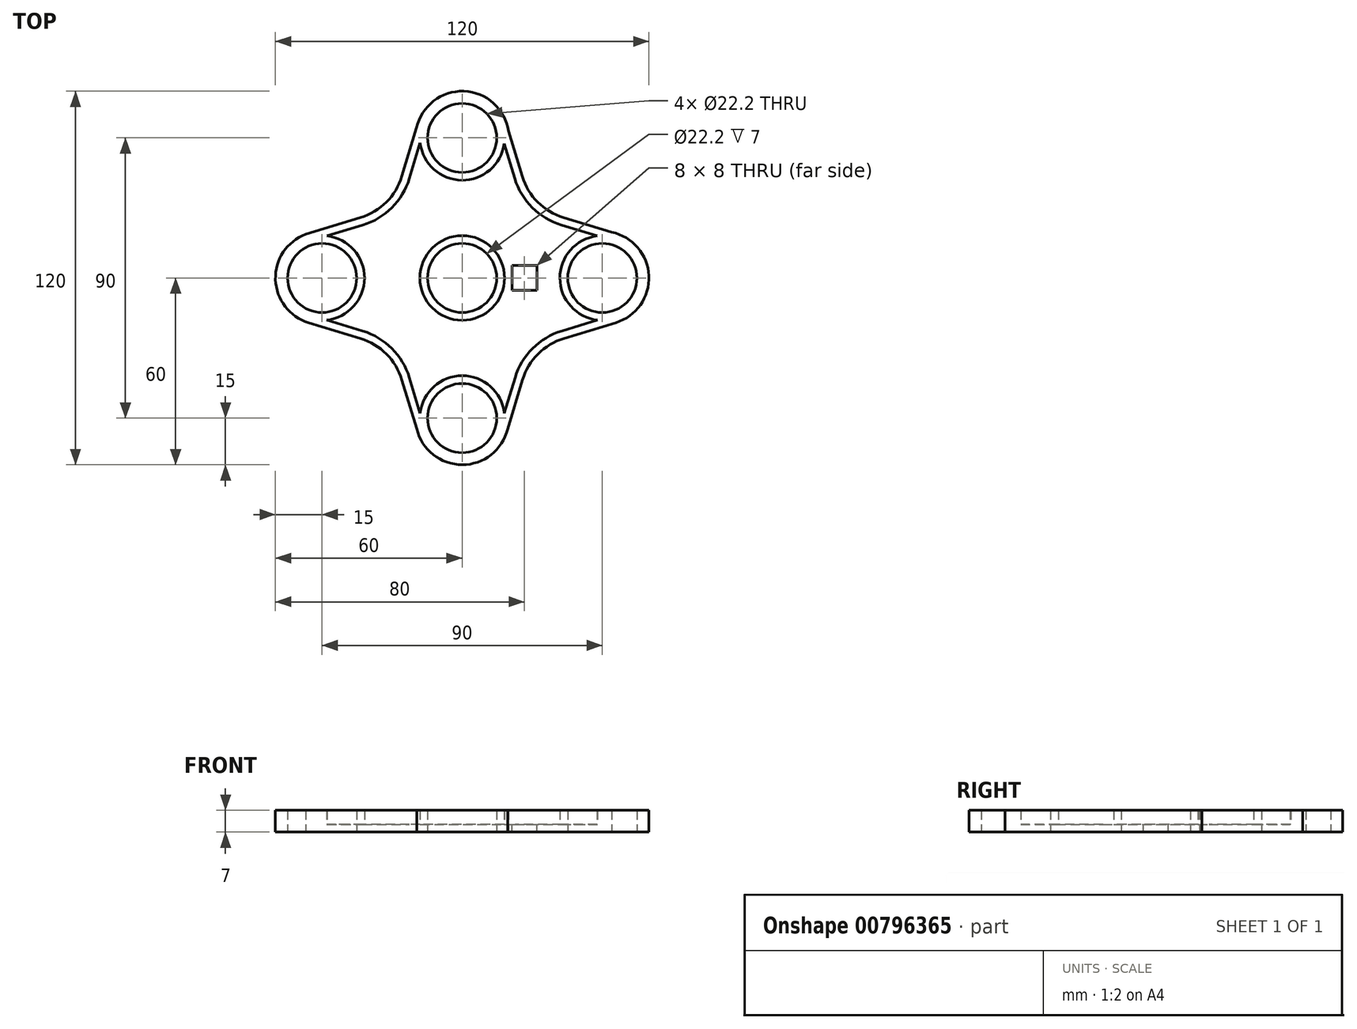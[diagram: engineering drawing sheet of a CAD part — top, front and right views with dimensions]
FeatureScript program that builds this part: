
annotation { "Feature Type Name" : "Feature", "Feature Type Description" : "" }
export const myFeature = defineFeature(function(context is Context, id is Id, definition is map)
    precondition{}
    {
        {
            var Q0;
            Q0=qCreatedBy(makeId("Top.planeOp"),FACE);
            var sketch = newSketch(context, id + "F0", { "sketchPlane" : qUnion([Q0])});
            skCircle(sketch, "E0", {"center": v(0, 45) * mm, "radius": 11.1 * mm});
            skCircle(sketch, "E1.1.0", {"center": v(-45, 0) * mm, "radius": 11.1 * mm});
            skCircle(sketch, "E1.2.0", {"center": v(0, -45) * mm, "radius": 11.1 * mm});
            skCircle(sketch, "E1.3.0", {"center": v(45, 0) * mm, "radius": 11.1 * mm});
            skPoint(sketch, "E1.center", {"position": v(0, 0) * mm});
            skCircle(sketch, "E2", {"center": v(0, 0) * mm, "radius": 11.1 * mm});
            skCircle(sketch, "E3", {"center": v(0, 45) * mm, "radius": 15 * mm});
            skCircle(sketch, "E4.1.0", {"center": v(-45, 0) * mm, "radius": 15 * mm});
            skCircle(sketch, "E4.2.0", {"center": v(0, -45) * mm, "radius": 15 * mm});
            skCircle(sketch, "E4.3.0", {"center": v(45, 0) * mm, "radius": 15 * mm});
            skPoint(sketch, "E5.end.orphan", {"position": v(-45, -15) * mm});
            skPoint(sketch, "E6.orphan", {"position": v(5, -45) * mm});
            skPoint(sketch, "E7.end.orphan", {"position": v(45, -25) * mm});
            skPoint(sketch, "E7.start.orphan", {"position": v(29.26, -21.9) * mm});
            skPoint(sketch, "E8.orphan", {"position": v(-30, 0) * mm});
            skPoint(sketch, "E9.orphan", {"position": v(0, -29.26) * mm});
            skPoint(sketch, "E10.orphan", {"position": v(29.32, 0) * mm});
            skLineSegment(sketch, "E11", {"start": v(-50.32, 14.03) * mm, "end": v(-32.69, 19.39) * mm});
            skLineSegment(sketch, "E12", {"start": v(-14.65, 48.2) * mm, "end": v(-19.37, 32.7) * mm});
            skPoint(sketch, "E13.orphan", {"position": v(-30, -2.23) * mm});
            skLineSegment(sketch, "E14", {"start": v(14.84, 47.16) * mm, "end": v(19.3, 32.66) * mm});
            skLineSegment(sketch, "E15", {"start": v(48.01, 14.7) * mm, "end": v(32.58, 19.4) * mm});
            skPoint(sketch, "E16.end.orphan", {"position": v(0, 30) * mm});
            skPoint(sketch, "E17.visualSharp", {"position": v(-22.48, 22.49) * mm});
            skArc(sketch, "E17.filletArc", {"start": v(-32.69, 19.39) * mm, "mid": v(-24.36, 24.38) * mm, "end": v(-19.37, 32.7) * mm});
            skPoint(sketch, "E18.visualSharp", {"position": v(22.4, 22.5) * mm});
            skArc(sketch, "E18.filletArc", {"start": v(19.3, 32.66) * mm, "mid": v(24.28, 24.37) * mm, "end": v(32.58, 19.4) * mm});
            skPoint(sketch, "E19.visualSharp", {"position": v(26.06, -10.75) * mm});
            skLineSegment(sketch, "E20", {"start": v(-32.68, -19.43) * mm, "end": v(-49.37, -14.35) * mm});
            skLineSegment(sketch, "E21", {"start": v(-14.6, -48.47) * mm, "end": v(-19.37, -32.75) * mm});
            skPoint(sketch, "E22.orphan", {"position": v(-30, 2.23) * mm});
            skLineSegment(sketch, "E23", {"start": v(14.58, -48.5) * mm, "end": v(19.38, -32.74) * mm});
            skLineSegment(sketch, "E24.trimOffspring", {"start": v(32.7, -19.41) * mm, "end": v(49.36, -14.35) * mm});
            skPoint(sketch, "E25.visualSharp", {"position": v(-22.47, -22.54) * mm});
            skArc(sketch, "E25.filletArc", {"start": v(-19.37, -32.75) * mm, "mid": v(-24.36, -24.42) * mm, "end": v(-32.68, -19.43) * mm});
            skPoint(sketch, "E26.visualSharp", {"position": v(22.48, -22.52) * mm});
            skArc(sketch, "E26.filletArc", {"start": v(32.7, -19.41) * mm, "mid": v(24.37, -24.4) * mm, "end": v(19.38, -32.74) * mm});
            skSolve(sketch);
        }
        {
            var Q0;
            Q0=makeQuery(id+"F0.imprint","IMPRINT",FACE,{"disambiguationData":[TD([[makeQuery(id+"F0.imprint","IMPRINT",EDGE,{"derivedFrom":sQuery(id+"F0.wireOp",EDGE,"E2")}),-1.0]])]});
            var Q1;
            Q1=makeQuery(id+"F0.imprint","IMPRINT",FACE,{"disambiguationData":[TD([[makeQuery(id+"F0.imprint","IMPRINT",EDGE,{"derivedFrom":sQuery(id+"F0.wireOp",EDGE,"E0")}),-1.0]])]});
            var Q2;
            Q2=makeQuery(id+"F0.imprint","IMPRINT",FACE,{"disambiguationData":[TD([[makeQuery(id+"F0.imprint","IMPRINT",EDGE,{"derivedFrom":sQuery(id+"F0.wireOp",EDGE,"E1.3.0")}),-1.0]])]});
            var Q3;
            Q3=makeQuery(id+"F0.imprint","IMPRINT",FACE,{"disambiguationData":[TD([[makeQuery(id+"F0.imprint","IMPRINT",EDGE,{"derivedFrom":sQuery(id+"F0.wireOp",EDGE,"E1.2.0")}),-1.0]])]});
            var Q4;
            Q4=makeQuery(id+"F0.imprint","IMPRINT",FACE,{"disambiguationData":[TD([[makeQuery(id+"F0.imprint","IMPRINT",EDGE,{"derivedFrom":sQuery(id+"F0.wireOp",EDGE,"E1.1.0")}),-1.0]])]});
            extrude(context, id + "F1", {"entities" : qUnion([Q0, Q1, Q2, Q3, Q4]), "endBound" : BoundingType.SYMMETRIC, "depth" : 7 * mm, "offsetDistance" : 25 * mm});
        }
        {
            var Q0;
            Q0=makeQuery(id+"F1.opExtrude","CAP_FACE",FACE,{"disambiguationData":[OSD([sQuery(id+"F0.wireOp",EDGE,"E0"),sQuery(id+"F0.wireOp",EDGE,"E1.1.0"),sQuery(id+"F0.wireOp",EDGE,"E1.2.0"),sQuery(id+"F0.wireOp",EDGE,"E1.3.0"),sQuery(id+"F0.wireOp",EDGE,"E2"),sQuery(id+"F0.wireOp",EDGE,"E3"),sQuery(id+"F0.wireOp",EDGE,"E4.1.0"),sQuery(id+"F0.wireOp",EDGE,"E4.2.0"),sQuery(id+"F0.wireOp",EDGE,"E4.3.0"),sQuery(id+"F0.wireOp",EDGE,"E5"),sQuery(id+"F0.wireOp",EDGE,"0SJW22FU-oLot-oJRP-qKUF-aOzY3QIeVuwd"),sQuery(id+"F0.wireOp",EDGE,"fu5gkHUn-R5B5-QnFn-U92b-98qJNMSDOywM"),sQuery(id+"F0.wireOp",EDGE,"cYeF52Lq-gdGK-U8gF-qFSO-TeWNDZtSGlOc"),sQuery(id+"F0.wireOp",EDGE,"SRZQqmhe-cdYh-si5h-Gv63-XMdrQUH1XgXB"),sQuery(id+"F0.wireOp",EDGE,"6NehxX5M-JFoF-wjyW-tTP8-N3nrQwtgs5PB"),sQuery(id+"F0.wireOp",EDGE,"jR7CxJDc-FOyD-6FGn-XZj9-uRTVhSQOKX0k"),sQuery(id+"F0.wireOp",EDGE,"E7")])],"isStart":false});
            shell(context, id + "F2", {"entities" : qUnion([Q0]), "thickness" : 2.5 * mm});
        }
        {
            var Q0;
            {var subQ0=sQuery(id+"F0.wireOp",EDGE,"E7");var subQ1=sQuery(id+"F0.wireOp",EDGE,"jR7CxJDc-FOyD-6FGn-XZj9-uRTVhSQOKX0k");var subQ2=sQuery(id+"F0.wireOp",EDGE,"6NehxX5M-JFoF-wjyW-tTP8-N3nrQwtgs5PB");var subQ3=sQuery(id+"F0.wireOp",EDGE,"SRZQqmhe-cdYh-si5h-Gv63-XMdrQUH1XgXB");var subQ4=sQuery(id+"F0.wireOp",EDGE,"cYeF52Lq-gdGK-U8gF-qFSO-TeWNDZtSGlOc");var subQ5=sQuery(id+"F0.wireOp",EDGE,"fu5gkHUn-R5B5-QnFn-U92b-98qJNMSDOywM");var subQ6=sQuery(id+"F0.wireOp",EDGE,"0SJW22FU-oLot-oJRP-qKUF-aOzY3QIeVuwd");var subQ7=sQuery(id+"F0.wireOp",EDGE,"E5");var subQ8=sQuery(id+"F0.wireOp",EDGE,"E4.3.0");var subQ9=sQuery(id+"F0.wireOp",EDGE,"E4.2.0");var subQ10=sQuery(id+"F0.wireOp",EDGE,"E4.1.0");var subQ11=sQuery(id+"F0.wireOp",EDGE,"E3");var subQ12=sQuery(id+"F0.wireOp",EDGE,"E2");var subQ13=sQuery(id+"F0.wireOp",EDGE,"E1.3.0");var subQ14=sQuery(id+"F0.wireOp",EDGE,"E1.2.0");var subQ15=sQuery(id+"F0.wireOp",EDGE,"E1.1.0");var subQ16=sQuery(id+"F0.wireOp",EDGE,"E0");Q0=makeQuery(id+"F2.opShell","OFFSET_FACE",FACE,{"disambiguationData":[OSD([subQ16,subQ15,subQ14,subQ13,subQ12,subQ11,subQ10,subQ9,subQ8,subQ7,subQ6,subQ5,subQ4,subQ3,subQ2,subQ1,subQ0]),TDD([makeQuery(id+"F1.opExtrude","CAP_FACE",FACE,{"disambiguationData":[OSD([subQ16,subQ15,subQ14,subQ13,subQ12,subQ11,subQ10,subQ9,subQ8,subQ7,subQ6,subQ5,subQ4,subQ3,subQ2,subQ1,subQ0])],"isStart":true})])]});}
            var sketch = newSketch(context, id + "F3", { "sketchPlane" : qUnion([Q0])});
            skLineSegment(sketch, "E27.bottom", {"start": v(16, 4) * mm, "end": v(24, 4) * mm});
            skLineSegment(sketch, "E27.top", {"start": v(16, -4) * mm, "end": v(24, -4) * mm});
            skLineSegment(sketch, "E27.left", {"start": v(16, 4) * mm, "end": v(16, -4) * mm});
            skLineSegment(sketch, "E27.right", {"start": v(24, 4) * mm, "end": v(24, -4) * mm});
            skPoint(sketch, "E27.middle", {"position": v(20, 0) * mm});
            skSolve(sketch);
        }
        {
            var Q0;
            Q0 = qSketchRegion(id + "F3", true);
            extrude(context, id + "F4", {"entities" : qUnion([Q0]), "operationType" : NewBodyOperationType.REMOVE, "oppositeDirection" : true, "depth" : 25 * mm, "offsetDistance" : 25 * mm});
        }
    });
